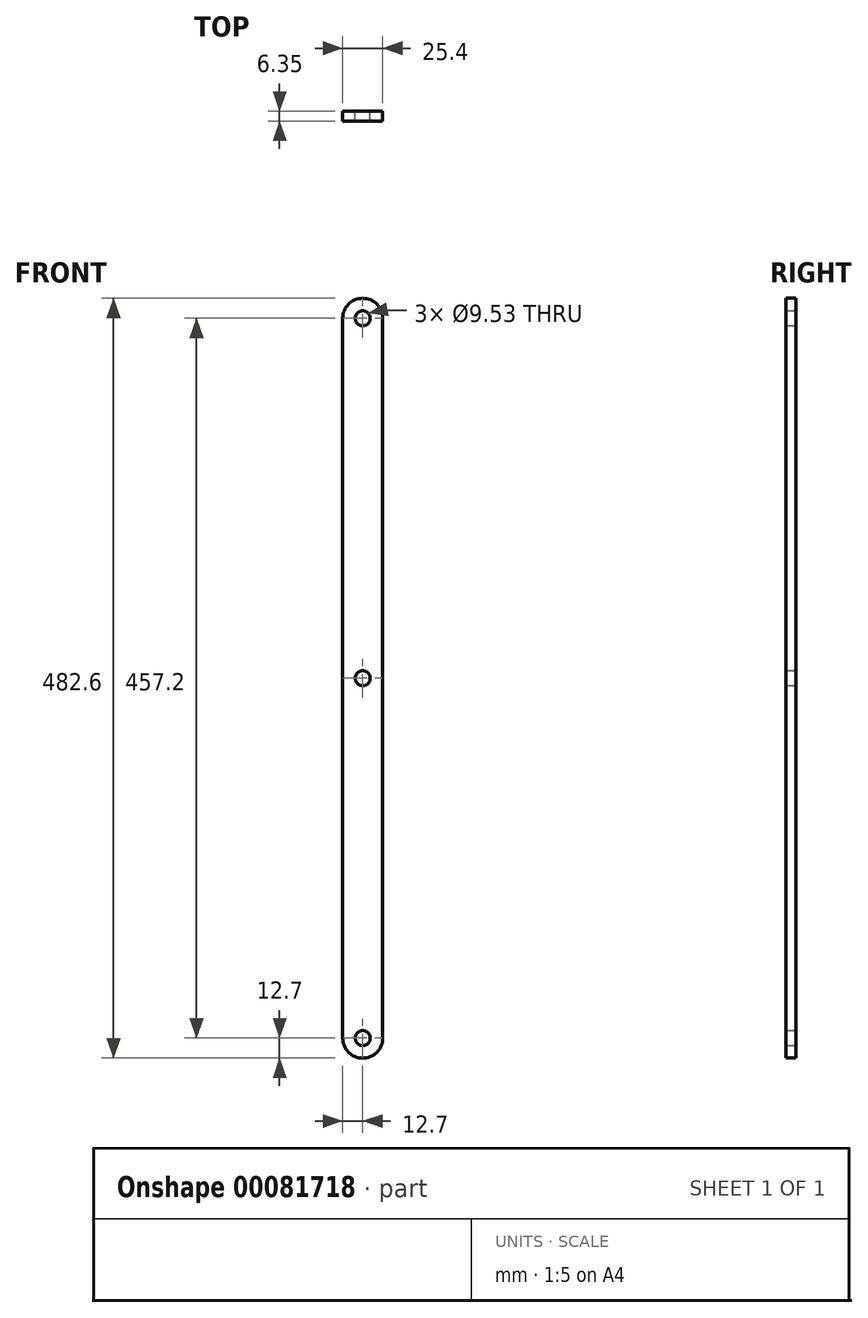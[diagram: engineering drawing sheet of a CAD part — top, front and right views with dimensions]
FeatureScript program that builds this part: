
annotation { "Feature Type Name" : "Feature", "Feature Type Description" : "" }
export const myFeature = defineFeature(function(context is Context, id is Id, definition is map)
    precondition{}
    {
        {
            var Q0;
            Q0=qCreatedBy(makeId("Front.planeOp"),FACE);
            var sketch = newSketch(context, id + "F0", { "sketchPlane" : qUnion([Q0])});
            skLineSegment(sketch, "E0", {"start": v(0, 0) * mm, "end": v(0, -457.2) * mm});
            skArc(sketch, "E1", {"start": v(0, -457.2) * mm, "mid": v(12.7, -469.9) * mm, "end": v(25.4, -457.2) * mm});
            skArc(sketch, "E2", {"start": v(0, 0) * mm, "mid": v(12.7, 12.7) * mm, "end": v(25.4, 0) * mm});
            skLineSegment(sketch, "E3", {"start": v(25.4, 0) * mm, "end": v(25.4, -457.2) * mm});
            skCircle(sketch, "E4", {"center": v(12.7, -457.2) * mm, "radius": 4.76 * mm});
            skCircle(sketch, "E5", {"center": v(12.7, 0) * mm, "radius": 4.76 * mm});
            skCircle(sketch, "E6", {"center": v(12.7, -228.6) * mm, "radius": 4.76 * mm});
            skPoint(sketch, "E6.centerSnap0", {"position": v(25.4, -228.6) * mm});
            skSolve(sketch);
        }
        {
            var Q0;
            Q0=makeQuery(id+"F0.imprint","IMPRINT",FACE,{"disambiguationData":[TD([[makeQuery(id+"F0.imprint","IMPRINT",EDGE,{"derivedFrom":sQuery(id+"F0.wireOp",EDGE,"E0")}),1.0]])]});
            extrude(context, id + "F1", {"entities" : qUnion([Q0]), "depth" : 6.35 * mm});
        }
    });
